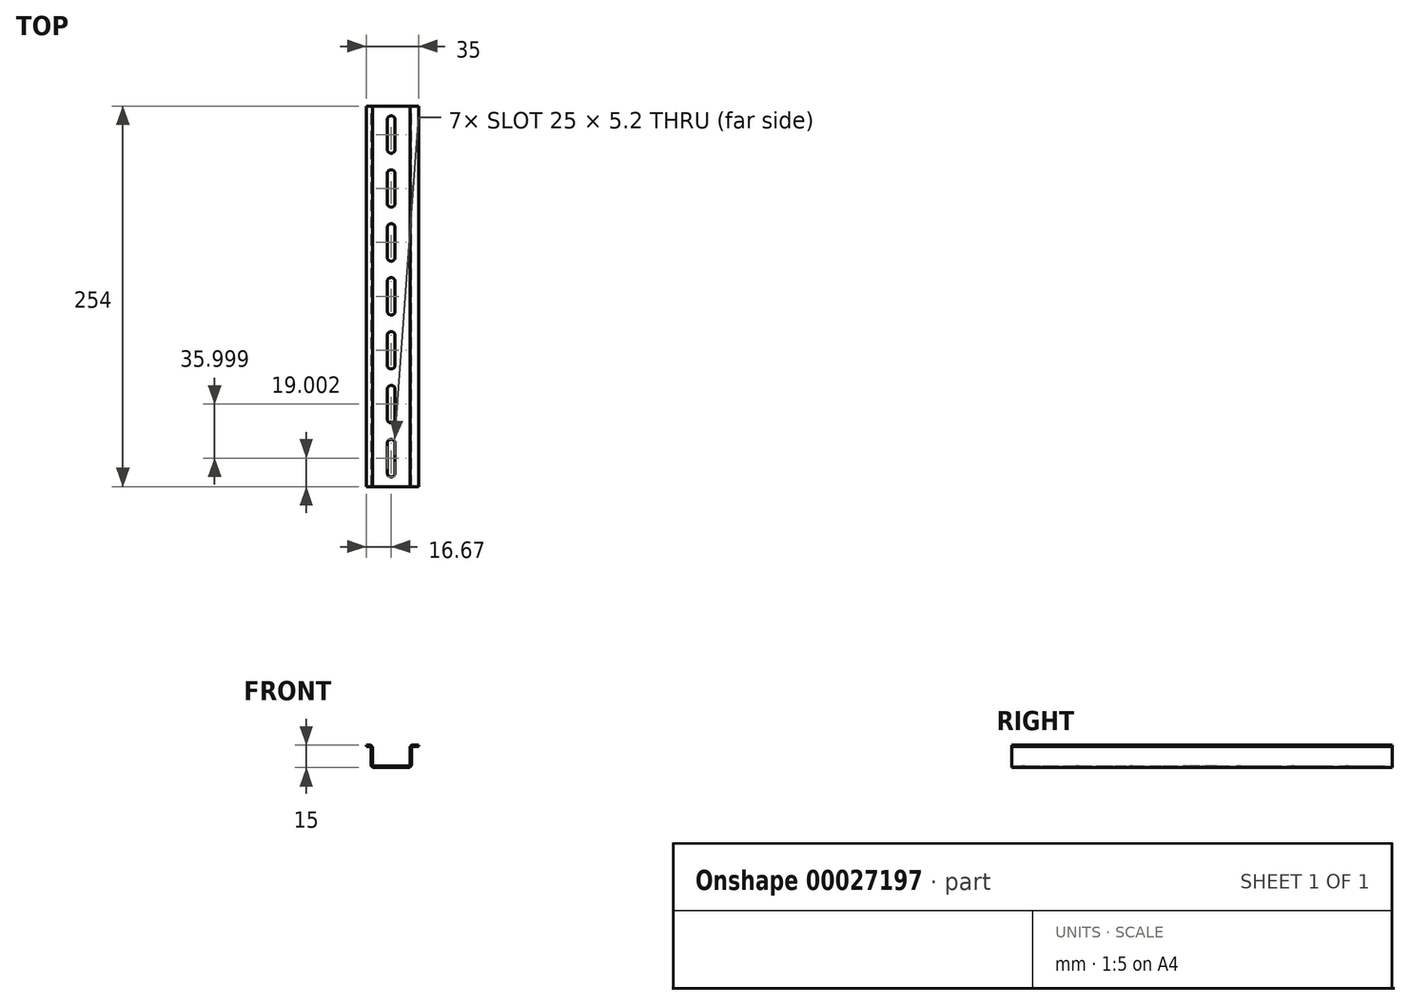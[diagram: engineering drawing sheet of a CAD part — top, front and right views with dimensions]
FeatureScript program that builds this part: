
annotation { "Feature Type Name" : "Feature", "Feature Type Description" : "" }
export const myFeature = defineFeature(function(context is Context, id is Id, definition is map)
    precondition{}
    {
        {
            var Q0;
            Q0=qCreatedBy(makeId("Front.planeOp"),FACE);
            var sketch = newSketch(context, id + "F0", { "sketchPlane" : qUnion([Q0])});
            skLineSegment(sketch, "E0", {"start": v(-11.5, 0) * mm, "end": v(11.5, 0) * mm});
            skLineSegment(sketch, "E1", {"start": v(13.5, 2) * mm, "end": v(13.5, 13) * mm});
            skLineSegment(sketch, "E2", {"start": v(14.5, 14) * mm, "end": v(18.33, 14) * mm});
            skLineSegment(sketch, "E3", {"start": v(18.33, 14) * mm, "end": v(18.33, 15) * mm});
            skLineSegment(sketch, "E4", {"start": v(18.33, 15) * mm, "end": v(14.52, 15) * mm});
            skLineSegment(sketch, "E5", {"start": v(12.52, 13) * mm, "end": v(12.52, 2) * mm});
            skLineSegment(sketch, "E6", {"start": v(11.52, 1) * mm, "end": v(-11.48, 1) * mm});
            skLineSegment(sketch, "E7", {"start": v(-12.48, 2) * mm, "end": v(-12.48, 13) * mm});
            skLineSegment(sketch, "E8", {"start": v(-14.48, 15) * mm, "end": v(-16.67, 15) * mm});
            skLineSegment(sketch, "E9", {"start": v(-16.67, 15) * mm, "end": v(-16.67, 14) * mm});
            skLineSegment(sketch, "E10", {"start": v(-16.67, 14) * mm, "end": v(-14.5, 14) * mm});
            skLineSegment(sketch, "E11", {"start": v(-13.5, 13) * mm, "end": v(-13.5, 2) * mm});
            skPoint(sketch, "E12.visualSharp", {"position": v(-12.48, 1) * mm});
            skArc(sketch, "E12.filletArc", {"start": v(-12.48, 2) * mm, "mid": v(-12.2, 1.3) * mm, "end": v(-11.48, 1) * mm});
            skPoint(sketch, "E13.visualSharp", {"position": v(12.52, 1) * mm});
            skArc(sketch, "E13.filletArc", {"start": v(11.52, 1) * mm, "mid": v(12.22, 1.3) * mm, "end": v(12.52, 2) * mm});
            skPoint(sketch, "E14.visualSharp", {"position": v(13.5, 14) * mm});
            skArc(sketch, "E14.filletArc", {"start": v(14.5, 14) * mm, "mid": v(13.8, 13.7) * mm, "end": v(13.5, 13) * mm});
            skPoint(sketch, "E15.visualSharp", {"position": v(-13.5, 14) * mm});
            skArc(sketch, "E15.filletArc", {"start": v(-13.5, 13) * mm, "mid": v(-13.8, 13.7) * mm, "end": v(-14.5, 14) * mm});
            skPoint(sketch, "E16.visualSharp", {"position": v(12.52, 15) * mm});
            skArc(sketch, "E16.filletArc", {"start": v(14.52, 15) * mm, "mid": v(13.1, 14.41) * mm, "end": v(12.52, 13) * mm});
            skPoint(sketch, "E17.visualSharp", {"position": v(13.5, 0) * mm});
            skArc(sketch, "E17.filletArc", {"start": v(11.5, 0) * mm, "mid": v(12.91, 0.59) * mm, "end": v(13.5, 2) * mm});
            skPoint(sketch, "E18.visualSharp", {"position": v(-13.5, 0) * mm});
            skArc(sketch, "E18.filletArc", {"start": v(-13.5, 2) * mm, "mid": v(-12.91, 0.59) * mm, "end": v(-11.5, 0) * mm});
            skPoint(sketch, "E19.visualSharp", {"position": v(-12.48, 15) * mm});
            skArc(sketch, "E19.filletArc", {"start": v(-12.48, 13) * mm, "mid": v(-13.07, 14.41) * mm, "end": v(-14.48, 15) * mm});
            skSolve(sketch);
        }
        {
            var Q0;
            Q0=qSketchRegion(id+"F0",true);
            extrude(context, id + "F1", {"entities" : qUnion([Q0]), "endBound" : BoundingType.SYMMETRIC, "depth" : 254 * mm});
        }
        {
            var Q0;
            Q0=makeQuery(id+"F1.opExtrude","SWEPT_FACE",FACE,{"disambiguationData":[OSD([sQuery(id+"F0.wireOp",EDGE,"E6")])]});
            var sketch = newSketch(context, id + "F2", { "sketchPlane" : qUnion([Q0])});
            skLineSegment(sketch, "E20", {"start": v(-2.6, 9.9) * mm, "end": v(-2.6, -9.9) * mm});
            skArc(sketch, "E21", {"start": v(-2.6, -9.9) * mm, "mid": v(0, -12.5) * mm, "end": v(2.6, -9.9) * mm});
            skLineSegment(sketch, "E22", {"start": v(2.6, -9.9) * mm, "end": v(2.6, 9.9) * mm});
            skArc(sketch, "E23", {"start": v(2.6, 9.9) * mm, "mid": v(0, 12.5) * mm, "end": v(-2.6, 9.9) * mm});
            skLineSegment(sketch, "E24", {"start": v(2.6, 26.1) * mm, "end": v(2.6, 45.9) * mm});
            skLineSegment(sketch, "E25", {"start": v(-2.6, 45.9) * mm, "end": v(-2.6, 26.1) * mm});
            skArc(sketch, "E26", {"start": v(2.6, 45.9) * mm, "mid": v(0, 48.5) * mm, "end": v(-2.6, 45.9) * mm});
            skArc(sketch, "E27", {"start": v(-2.6, 26.1) * mm, "mid": v(0, 23.5) * mm, "end": v(2.6, 26.1) * mm});
            skLineSegment(sketch, "E28", {"start": v(2.6, 62.1) * mm, "end": v(2.6, 81.9) * mm});
            skLineSegment(sketch, "E29", {"start": v(-2.6, 81.9) * mm, "end": v(-2.6, 62.1) * mm});
            skArc(sketch, "E30", {"start": v(2.6, 81.9) * mm, "mid": v(0, 84.5) * mm, "end": v(-2.6, 81.9) * mm});
            skArc(sketch, "E31", {"start": v(-2.6, 62.1) * mm, "mid": v(0, 59.5) * mm, "end": v(2.6, 62.1) * mm});
            skLineSegment(sketch, "E32", {"start": v(2.6, 98.1) * mm, "end": v(2.6, 117.9) * mm});
            skLineSegment(sketch, "E33", {"start": v(-2.6, 117.9) * mm, "end": v(-2.6, 98.1) * mm});
            skArc(sketch, "E34", {"start": v(2.6, 117.9) * mm, "mid": v(0, 120.5) * mm, "end": v(-2.6, 117.9) * mm});
            skArc(sketch, "E35", {"start": v(-2.6, 98.1) * mm, "mid": v(0, 95.5) * mm, "end": v(2.6, 98.1) * mm});
            skLineSegment(sketch, "E36", {"start": v(2.6, -45.9) * mm, "end": v(2.6, -26.1) * mm});
            skLineSegment(sketch, "E37", {"start": v(-2.6, -26.1) * mm, "end": v(-2.6, -45.9) * mm});
            skArc(sketch, "E38", {"start": v(2.6, -26.1) * mm, "mid": v(0, -23.5) * mm, "end": v(-2.6, -26.1) * mm});
            skArc(sketch, "E39", {"start": v(-2.6, -45.9) * mm, "mid": v(0, -48.5) * mm, "end": v(2.6, -45.9) * mm});
            skLineSegment(sketch, "E40", {"start": v(2.6, -81.9) * mm, "end": v(2.6, -62.1) * mm});
            skLineSegment(sketch, "E41", {"start": v(-2.6, -62.1) * mm, "end": v(-2.6, -81.9) * mm});
            skArc(sketch, "E42", {"start": v(2.6, -62.1) * mm, "mid": v(0, -59.5) * mm, "end": v(-2.6, -62.1) * mm});
            skArc(sketch, "E43", {"start": v(-2.6, -81.9) * mm, "mid": v(0, -84.5) * mm, "end": v(2.6, -81.9) * mm});
            skLineSegment(sketch, "E44", {"start": v(2.6, -117.9) * mm, "end": v(2.6, -98.1) * mm});
            skLineSegment(sketch, "E45", {"start": v(-2.6, -98.1) * mm, "end": v(-2.6, -117.9) * mm});
            skArc(sketch, "E46", {"start": v(2.6, -98.1) * mm, "mid": v(0, -95.5) * mm, "end": v(-2.6, -98.1) * mm});
            skArc(sketch, "E47", {"start": v(-2.6, -117.9) * mm, "mid": v(0, -120.5) * mm, "end": v(2.6, -117.9) * mm});
            skSolve(sketch);
        }
        {
            var Q0;
            Q0=qSketchRegion(id+"F2",true);
            extrude(context, id + "F3", {"entities" : qUnion([Q0]), "operationType" : NewBodyOperationType.REMOVE, "endBound" : BoundingType.THROUGH_ALL, "oppositeDirection" : true, "depth" : 25.4 * mm});
        }
    });
